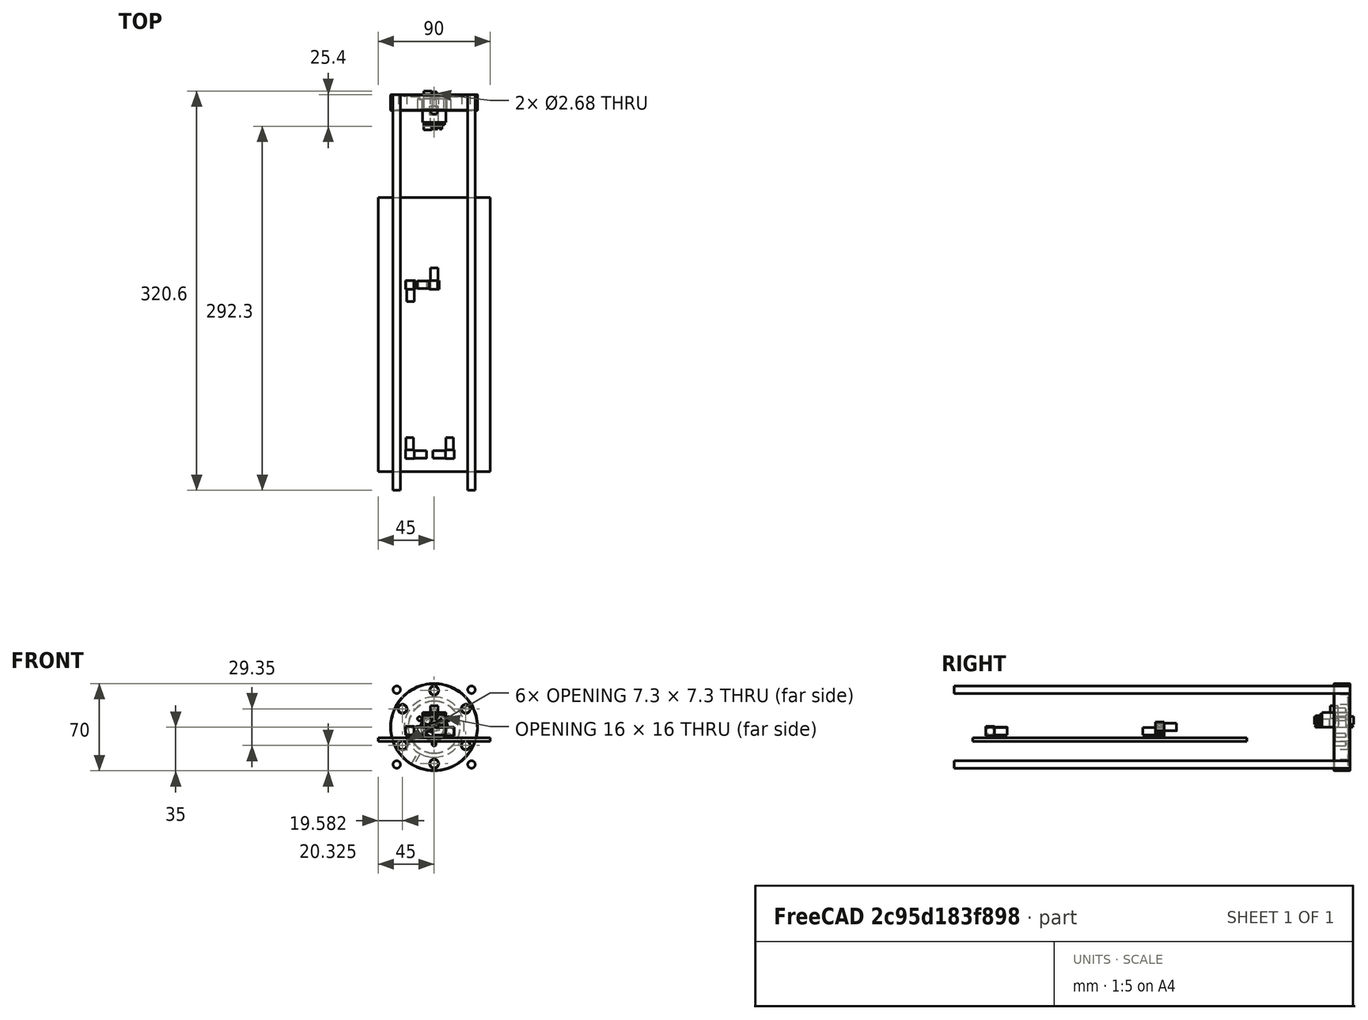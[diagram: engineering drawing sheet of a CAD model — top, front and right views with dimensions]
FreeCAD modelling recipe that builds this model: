
FCSTD DOCUMENT  (FreeCAD 0.20R29603 (Git))
Label: MechanicalCF35Mount_Assembly
License: All rights reserved
LicenseURL: http://en.wikipedia.org/wiki/All_rights_reserved
objects: Part::Feature×22, App::Link×16, Part::Compound×9, Part::Cylinder×4, Part::Box×1
note: 36 computed .brp shape members not serialized (recipe doc carries the construction recipe); baked Part::Feature solids carry a one-line shape summary decoded from their .brp
EXTERNAL_REF file=MechanicalCF35Mount001.FCStd obj=Fillet_solid
EXTERNAL_REF file=MechanicalCF35Mount002.FCStd obj=Cut001_solid
EXTERNAL_REF file=MechanicalCF35Mount003.FCStd obj=Cut001_solid
EXTERNAL_REF file=MechanicalCF35Mount004.FCStd obj=Cut_solid
EXTERNAL_REF file=../../MiniCircuits/GC957.FCStd obj=Fusion001_solid
EXTERNAL_REF file=../../MiniCircuits/FF99.FCStd obj=Fusion_solid
EXTERNAL_REF file=../../MiniCircuits/SMA-L.FCStd obj=Fusion_solid
EXTERNAL_REF file=MechanicalCF35Mount005.FCStd obj=Common_solid

FEATURE [App::Link] Link  label="Frontplane"
  LinkedObject = -> <external MechanicalCF35Mount001.FCStd>#Fillet_solid
FEATURE [Part::Cylinder] Cylinder  label="Zylinder"
  Angle = 360
  AttacherType = Attacher::AttachEngine3D
  FirstAngle = 0
  Height = 317.7
  Placement = pos=(-30,12.7,-30) rot=(1,0,0;1.5708rad)
  Radius = 3
  SecondAngle = 0
FEATURE [Part::Cylinder] Cylinder001  label="Zylinder001"
  Angle = 360
  AttacherType = Attacher::AttachEngine3D
  FirstAngle = 0
  Height = 317.7
  Placement = pos=(-30,12.7,-30) rot=(1,0,0;1.5708rad)
  Radius = 3
  SecondAngle = 0
FEATURE [Part::Compound] Compound
  Links = -> [Cylinder001]
  Placement = pos=(0,0,0) rot=(0,1,0;1.5708rad)
FEATURE [Part::Cylinder] Cylinder002  label="Zylinder002"
  Angle = 360
  AttacherType = Attacher::AttachEngine3D
  FirstAngle = 0
  Height = 317.7
  Placement = pos=(-30,12.7,-30) rot=(1,0,0;1.5708rad)
  Radius = 3
  SecondAngle = 0
FEATURE [Part::Compound] Compound001
  Links = -> [Cylinder002]
  Placement = pos=(0,0,0) rot=(0,1,0;3.14159rad)
FEATURE [Part::Cylinder] Cylinder003  label="Zylinder003"
  Angle = 360
  AttacherType = Attacher::AttachEngine3D
  FirstAngle = 0
  Height = 317.7
  Placement = pos=(-30,12.7,-30) rot=(1,0,0;1.5708rad)
  Radius = 3
  SecondAngle = 0
FEATURE [Part::Compound] Compound002
  Links = -> [Cylinder003]
  Placement = pos=(0,0,0) rot=(0,1,0;4.71239rad)
FEATURE [Part::Compound] Compound003  label="ThreadedRodsM6"
  Links = -> [Compound002,Compound,Compound001,Cylinder]
FEATURE [App::Link] Link005  label="Backplane"
  LinkPlacement = pos=(0,-302,0) rot=(0,0,1;0rad)
  LinkedObject = -> <external MechanicalCF35Mount002.FCStd>#Cut001_solid
  Placement = pos=(0,-302,0) rot=(0,0,1;0rad)
FEATURE [App::Link] Link006  label="Coversheet"
  LinkedObject = -> <external MechanicalCF35Mount003.FCStd>#Cut001_solid
FEATURE [App::Link] Link007  label="Bottomplane"
  LinkPlacement = pos=(0,0,-101.8) rot=(0,0,1;0rad)
  LinkedObject = -> <external MechanicalCF35Mount004.FCStd>#Cut_solid
  Placement = pos=(0,0,-101.8) rot=(0,0,1;0rad)
FEATURE [Part::Feature] Solid  label="Hositrad_CFA35-16D"
  shape: bbox 70 x 12.7 x 70 mm, 88 faces (baked)
FEATURE [Part::Feature] _7192_01_CF
  shape: bbox 33.78 x 40.23 x 14.22 mm, 39 faces, 0 solids (baked)
FEATURE [Part::Feature] _7192_01_CF001
  Placement = pos=(0,0,-39.0113) rot=(1,0,0;1.5708rad)
  shape: bbox 14 x 7.506 x 26.34 mm, 46 faces, 0 solids (baked)
FEATURE [Part::Feature] _7192_01_CF002
  Placement = pos=(0,0,-58.2625) rot=(-0.03621,0.706643,0.706643;3.21398rad)
  shape: bbox 18.12 x 10.39 x 7.838 mm, 29 faces, 0 solids (baked)
FEATURE [Part::Feature] _7192_01_CF003
  Placement = pos=(0,0,-42.2965) rot=(0.8891,-0.323652,-0.323652;1.68807rad)
  shape: bbox 16.99 x 16.03 x 5.603 mm, 25 faces, 0 solids (baked)
FEATURE [Part::Feature] _7192_01_CF004
  Placement = pos=(0,0,-35.56) rot=(0,0.707107,-0.707107;3.14159rad)
  shape: bbox 22.78 x 12.72 x 33.85 mm, 35 faces, 0 solids (baked)
FEATURE [Part::Feature] _7192_01_CF005
  Placement = pos=(0,0,-36.7339) rot=(0.997746,-0.047454,-0.047454;1.57305rad)
  shape: bbox 7.007 x 7.007 x 0.8128 mm, 6 faces, 0 solids (baked)
FEATURE [Part::Feature] _7192_01_CF006
  Placement = pos=(0,0,-66.0654) rot=(0.57735,0.57735,0.57735;2.0944rad)
  shape: bbox 2.416 x 2.416 x 39.37 mm, 29 faces, 0 solids (baked)
FEATURE [Part::Feature] _7192_01_CF007
  Placement = pos=(0,0,-32.2253) rot=(-0.196732,-0.693288,0.693288;2.75309rad)
  shape: bbox 26.96 x 26.96 x 13.28 mm, 55 faces, 0 solids (baked)
FEATURE [Part::Feature] _7192_01_CF008
  Placement = pos=(0,0,-46.1699) rot=(-0.196732,-0.693288,0.693288;2.75309rad)
  shape: bbox 34.28 x 29.27 x 4.775 mm, 16 faces, 0 solids (baked)
FEATURE [Part::Feature] _7192_01_CF009
  Placement = pos=(0,0,-22.86) rot=(-0.196732,-0.693288,0.693288;2.75309rad)
  shape: bbox 24.3 x 24.3 x 12.6 mm, 19 faces, 0 solids (baked)
FEATURE [Part::Feature] _7192_01_CF010
  Placement = pos=(0,0,-12.7) rot=(-0.196732,-0.693288,0.693288;2.75309rad)
  shape: bbox 26.42 x 26.42 x 12.7 mm, 14 faces, 0 solids (baked)
FEATURE [Part::Feature] _7192_01_CF011
  Placement = pos=(0,0,-42.1821) rot=(-0.196732,-0.693288,0.693288;2.75309rad)
  shape: bbox 43.95 x 37.52 x 5.044 mm, 27 faces, 0 solids (baked)
FEATURE [Part::Feature] _7192_01_CF012
  Placement = pos=(0,0,-35.56) rot=(0.079728,0.704856,0.704856;2.98247rad)
  shape: bbox 15.4 x 15.4 x 39.12 mm, 6 faces, 0 solids (baked)
FEATURE [Part::Feature] _7192_01_CF013
  Placement = pos=(0,0,-26.6954) rot=(0.165786,0.697322,0.697322;2.81301rad)
  shape: bbox 5.339 x 4.281 x 34.06 mm, 6 faces, 0 solids (baked)
FEATURE [Part::Feature] _7192_01_CF014
  Placement = pos=(0,0,6.7564) rot=(0.205998,0.691941,-0.691941;3.54791rad)
  shape: bbox 9.907 x 7.446 x 1.311 mm, 4 faces, 0 solids (baked)
FEATURE [Part::Feature] _7192_01_CF015
  Placement = pos=(0,0,-7.9756) rot=(1,0,0;1.5708rad)
  shape: bbox 22.78 x 12.72 x 22.32 mm, 35 faces, 0 solids (baked)
FEATURE [Part::Feature] _7192_01_CF016
  Placement = pos=(0,0,22.3805) rot=(0.205998,0.691941,-0.691941;3.54791rad)
  shape: bbox 3.344 x 3.344 x 15.27 mm, 29 faces, 0 solids (baked)
FEATURE [Part::Feature] _7192_01_CF017
  Placement = pos=(0,0,6.7564) rot=(1,0,0;1.5708rad)
  shape: bbox 10.8 x 10.8 x 1.524 mm, 10 faces, 0 solids (baked)
FEATURE [Part::Compound] Compound004  label="CF16BNCFeedthrough"
  Links = -> [_7192_01_CF,_7192_01_CF001,_7192_01_CF002,_7192_01_CF003,_7192_01_CF004,_7192_01_CF005,_7192_01_CF006,_7192_01_CF007,_7192_01_CF008,_7192_01_CF009,_7192_01_CF010,_7192_01_CF011,_7192_01_CF012,_7192_01_CF013,_7192_01_CF014,_7192_01_CF015,_7192_01_CF016,_7192_01_CF017]
  Placement = pos=(0,0,0) rot=(-1,0,0;1.5708rad)
FEATURE [App::Link] Link008  label="Preamp1"
  LinkPlacement = pos=(-14.5,-165,-8.45) rot=(0,0,1;0rad)
  LinkedObject = -> <external ../../MiniCircuits/GC957.FCStd>#Fusion001_solid
  Placement = pos=(-14.5,-165,-8.45) rot=(0,0,1;0rad)
FEATURE [App::Link] Link009  label="SHP-175"
  LinkPlacement = pos=(0,-86,0) rot=(1,0,0;1.5708rad)
  LinkedObject = -> <external ../../MiniCircuits/FF99.FCStd>#Fusion_solid
  Placement = pos=(0,-86,0) rot=(1,0,0;1.5708rad)
FEATURE [App::Link] Link010  label="Fusion (Solid)"
  LinkPlacement = pos=(0,-140,-3.5) rot=(0,0,1;3.14159rad)
  LinkedObject = -> <external ../../MiniCircuits/SMA-L.FCStd>#Fusion_solid
  Placement = pos=(0,-140,-3.5) rot=(0,0,1;3.14159rad)
FEATURE [Part::Compound] Compound005  label="SMAL001"
  Links = -> [Link010]
  Placement = pos=(0,0,0) rot=(0,-1,0;1.74533rad)
FEATURE [App::Link] Link011  label="Fusion (Solid)001"
  LinkPlacement = pos=(0,-140,-3.5) rot=(0,0,1;0rad)
  LinkedObject = -> Fusion_solid
  Placement = pos=(0,-140,-3.5) rot=(0,0,1;0rad)
FEATURE [Part::Compound] Compound006  label="SMAL002"
  Links = -> [Link011]
  Placement = pos=(-19,0,-3.45) rot=(0,1,0;1.39626rad)
FEATURE [Part::Feature] Fusion_solid  label="Fusion (Solid)002"
  shape: bbox 7 x 17 x 17 mm, 12 faces (baked)
FEATURE [App::Link] Link012  label="Preamp002"
  LinkPlacement = pos=(-14.5,-207,-8.45) rot=(0,0,1;0rad)
  LinkedObject = -> Fusion001_solid
  Placement = pos=(-14.5,-207,-8.45) rot=(0,0,1;0rad)
FEATURE [Part::Feature] Fusion001_solid  label="Fusion001 (Solid)"
  shape: bbox 18.8 x 31.2 x 11.61 mm, 42 faces (baked)
FEATURE [Part::Feature] Fusion001_solid001  label="Fusion001 (Solid)001"
  shape: bbox 18.8 x 31.2 x 11.61 mm, 42 faces (baked)
FEATURE [App::Link] Link013  label="Preamp003"
  LinkPlacement = pos=(-14.5,-248,-8.45) rot=(0,0,1;0rad)
  LinkedObject = -> Fusion001_solid001
  Placement = pos=(-14.5,-248,-8.45) rot=(0,0,1;0rad)
FEATURE [App::Link] Link014  label="Fusion (Solid)003"
  LinkPlacement = pos=(0,0,0) rot=(0,0,1;3.14159rad)
  LinkedObject = -> <external ../../MiniCircuits/SMA-L.FCStd>#Fusion_solid
  Placement = pos=(0,0,0) rot=(0,0,1;3.14159rad)
FEATURE [Part::Compound] Compound007  label="SMAL003"
  Links = -> [Link014]
  Placement = pos=(-23,-276,-3) rot=(0,1,0;1.5708rad)
FEATURE [App::Link] Link015  label="Fusion (Solid)004"
  LinkPlacement = pos=(0,0,0) rot=(0,1,0;1.5708rad)
  LinkedObject = -> <external ../../MiniCircuits/SMA-L.FCStd>#Fusion_solid
  Placement = pos=(0,0,0) rot=(0,1,0;1.5708rad)
FEATURE [Part::Compound] Compound008
  Links = -> [Link015]
  Placement = pos=(16,-276,-3.5) rot=(0,0,1;3.14159rad)
FEATURE [Part::Box] Box  label="MountBoard"
  AttacherType = Attacher::AttachEngine3D
  Height = 2.8
  Length = 90
  Placement = pos=(-45,-290,-11.5) rot=(0,0,1;0rad)
  Width = 220
FEATURE [App::Link] Link016  label="Common (Solid)"
  LinkPlacement = pos=(0,-76,0) rot=(0,0,1;0rad)
  LinkedObject = -> <external MechanicalCF35Mount005.FCStd>#Common_solid
  Placement = pos=(0,-76,0) rot=(0,0,1;0rad)
FEATURE [App::Link] Link017  label="Common (Solid)001"
  LinkPlacement = pos=(0,-283,0) rot=(0,0,1;0rad)
  LinkedObject = -> <external MechanicalCF35Mount005.FCStd>#Common_solid
  Placement = pos=(0,-283,0) rot=(0,0,1;0rad)
FEATURE [App::Link] Link018  label="Common (Solid)002"
  LinkPlacement = pos=(0,-144,0) rot=(0,0,1;0rad)
  LinkedObject = -> <external MechanicalCF35Mount005.FCStd>#Common_solid
  Placement = pos=(0,-144,0) rot=(0,0,1;0rad)
FEATURE [App::Link] Link019  label="Common (Solid)003"
  LinkPlacement = pos=(0,-215,0) rot=(0,0,1;0rad)
  LinkedObject = -> <external MechanicalCF35Mount005.FCStd>#Common_solid
  Placement = pos=(0,-215,0) rot=(0,0,1;0rad)

RESOLVED EXTERNAL PARTS (link-assembly join: the EXTERNAL_REF files above that resolve inside this repo's crawl, each included once):
---- part MechanicalCF35Mount001.FCStd = doc fcstd_43c363c283f8 ----
FCSTD DOCUMENT  (FreeCAD 0.20R29603 (Git))
Label: MechanicalCF35Mount001
License: All rights reserved
LicenseURL: http://en.wikipedia.org/wiki/All_rights_reserved
objects: Part::Feature×20, Part::Cylinder×15, TechDraw::DrawViewDimension×13, Part::Compound×12, TechDraw::DrawProjGroupItem×5, Part::Cut×4, Part::Box×1, Part::Fillet×1, TechDraw::DrawSVGTemplate×1, TechDraw::DrawProjGroup×1, TechDraw::DrawPage×1
note: 53 computed .brp shape members not serialized (recipe doc carries the construction recipe); baked Part::Feature solids carry a one-line shape summary decoded from their .brp

FEATURE [Part::Feature] Solid  label="Hositrad_CFA35-16D"
  shape: bbox 70 x 12.7 x 70 mm, 88 faces (baked)
FEATURE [Part::Feature] _7192_01_CF
  shape: bbox 33.78 x 40.23 x 14.22 mm, 39 faces, 0 solids (baked)
FEATURE [Part::Feature] _7192_01_CF001
  Placement = pos=(0,0,-39.0113) rot=(1,0,0;1.5708rad)
  shape: bbox 14 x 7.506 x 26.34 mm, 46 faces, 0 solids (baked)
FEATURE [Part::Feature] _7192_01_CF002
  Placement = pos=(0,0,-58.2625) rot=(-0.03621,0.706643,0.706643;3.21398rad)
  shape: bbox 18.12 x 10.39 x 7.838 mm, 29 faces, 0 solids (baked)
FEATURE [Part::Feature] _7192_01_CF003
  Placement = pos=(0,0,-42.2965) rot=(0.8891,-0.323652,-0.323652;1.68807rad)
  shape: bbox 16.99 x 16.03 x 5.603 mm, 25 faces, 0 solids (baked)
FEATURE [Part::Feature] _7192_01_CF004
  Placement = pos=(0,0,-35.56) rot=(0,0.707107,-0.707107;3.14159rad)
  shape: bbox 22.78 x 12.72 x 33.85 mm, 35 faces, 0 solids (baked)
FEATURE [Part::Feature] _7192_01_CF005
  Placement = pos=(0,0,-36.7339) rot=(0.997746,-0.047454,-0.047454;1.57305rad)
  shape: bbox 7.007 x 7.007 x 0.8128 mm, 6 faces, 0 solids (baked)
FEATURE [Part::Feature] _7192_01_CF006
  Placement = pos=(0,0,-66.0654) rot=(0.57735,0.57735,0.57735;2.0944rad)
  shape: bbox 2.416 x 2.416 x 39.37 mm, 29 faces, 0 solids (baked)
FEATURE [Part::Feature] _7192_01_CF007
  Placement = pos=(0,0,-32.2253) rot=(0.196732,0.693288,-0.693288;3.5301rad)
  shape: bbox 26.96 x 26.96 x 13.28 mm, 55 faces, 0 solids (baked)
FEATURE [Part::Feature] _7192_01_CF008
  Placement = pos=(0,0,-46.1699) rot=(0.196732,0.693288,-0.693288;3.5301rad)
  shape: bbox 34.28 x 29.27 x 4.775 mm, 16 faces, 0 solids (baked)
FEATURE [Part::Feature] _7192_01_CF009
  Placement = pos=(0,0,-22.86) rot=(0.196732,0.693288,-0.693288;3.5301rad)
  shape: bbox 24.3 x 24.3 x 12.6 mm, 19 faces, 0 solids (baked)
FEATURE [Part::Feature] _7192_01_CF010
  Placement = pos=(0,0,-12.7) rot=(0.196732,0.693288,-0.693288;3.5301rad)
  shape: bbox 26.42 x 26.42 x 12.7 mm, 14 faces, 0 solids (baked)
FEATURE [Part::Feature] _7192_01_CF011
  Placement = pos=(0,0,-42.1821) rot=(0.196732,0.693288,-0.693288;3.5301rad)
  shape: bbox 43.95 x 37.52 x 5.044 mm, 27 faces, 0 solids (baked)
FEATURE [Part::Feature] _7192_01_CF012
  Placement = pos=(0,0,-35.56) rot=(0.079728,0.704856,0.704856;2.98247rad)
  shape: bbox 15.4 x 15.4 x 39.12 mm, 6 faces, 0 solids (baked)
FEATURE [Part::Feature] _7192_01_CF013
  Placement = pos=(0,0,-26.6954) rot=(0.165786,0.697322,0.697322;2.81301rad)
  shape: bbox 5.339 x 4.281 x 34.06 mm, 6 faces, 0 solids (baked)
FEATURE [Part::Feature] _7192_01_CF014
  Placement = pos=(0,0,6.7564) rot=(0.205998,0.691941,-0.691941;3.54791rad)
  shape: bbox 9.907 x 7.446 x 1.311 mm, 4 faces, 0 solids (baked)
FEATURE [Part::Feature] _7192_01_CF015
  Placement = pos=(0,0,-7.9756) rot=(1,0,0;1.5708rad)
  shape: bbox 22.78 x 12.72 x 22.32 mm, 35 faces, 0 solids (baked)
FEATURE [Part::Feature] _7192_01_CF016
  Placement = pos=(0,0,22.3805) rot=(0.205998,0.691941,-0.691941;3.54791rad)
  shape: bbox 3.344 x 3.344 x 15.27 mm, 29 faces, 0 solids (baked)
FEATURE [Part::Feature] _7192_01_CF017
  Placement = pos=(0,0,6.7564) rot=(1,0,0;1.5708rad)
  shape: bbox 10.8 x 10.8 x 1.524 mm, 10 faces, 0 solids (baked)
FEATURE [Part::Compound] Compound  label="CF16BNCFeedthrough"
  Links = -> [_7192_01_CF,_7192_01_CF001,_7192_01_CF002,_7192_01_CF003,_7192_01_CF004,_7192_01_CF005,_7192_01_CF006,_7192_01_CF007,_7192_01_CF008,_7192_01_CF009,_7192_01_CF010,_7192_01_CF011,_7192_01_CF012,_7192_01_CF013,_7192_01_CF014,_7192_01_CF015,_7192_01_CF016,_7192_01_CF017]
  Placement = pos=(0,0,0) rot=(-1,0,0;1.5708rad)
FEATURE [Part::Box] Box  label="Würfel"
  AttacherType = Attacher::AttachEngine3D
  Height = 100
  Length = 100
  Placement = pos=(-50,0,-50) rot=(0,0,1;0rad)
  Width = 12.7
FEATURE [Part::Cylinder] Cylinder  label="Zylinder"
  Angle = 360
  AttacherType = Attacher::AttachEngine3D
  FirstAngle = 0
  Height = 12.7
  Placement = pos=(0,12.7,0) rot=(1,0,0;1.5708rad)
  Radius = 35.5
  SecondAngle = 0
FEATURE [Part::Cut] Cut
  Base = -> Box
  Tool = -> Cylinder
FEATURE [Part::Cylinder] Cylinder001  label="Zylinder001"
  Angle = 360
  AttacherType = Attacher::AttachEngine3D
  FirstAngle = 0
  Height = 100
  Placement = pos=(0,6.35,-50) rot=(0,0,1;0rad)
  Radius = 2.46
  SecondAngle = 0
FEATURE [Part::Cylinder] Cylinder002  label="Zylinder002"
  Angle = 360
  AttacherType = Attacher::AttachEngine3D
  FirstAngle = 0
  Height = 100
  Placement = pos=(0,6.35,-50) rot=(0,0,1;0rad)
  Radius = 2.46
  SecondAngle = 0
FEATURE [Part::Compound] Compound001
  Links = -> [Cylinder002]
  Placement = pos=(0,0,0) rot=(0,1,0;1.5708rad)
FEATURE [Part::Compound] Compound002  label="SetscrewCoreholes"
  Links = -> [Compound001,Cylinder001]
FEATURE [Part::Cut] Cut001
  Base = -> Cut
  Tool = -> Compound002
FEATURE [Part::Cylinder] Cylinder003  label="Zylinder003"
  Angle = 360
  AttacherType = Attacher::AttachEngine3D
  FirstAngle = 0
  Height = 12
  Placement = pos=(-30,6.3,-50) rot=(0,0,1;0rad)
  Radius = 2.46
  SecondAngle = 0
FEATURE [Part::Cylinder] Cylinder004  label="Zylinder004"
  Angle = 360
  AttacherType = Attacher::AttachEngine3D
  FirstAngle = 0
  Height = 12
  Placement = pos=(30,6.3,-50) rot=(0,0,1;0rad)
  Radius = 2.46
  SecondAngle = 0
FEATURE [Part::Compound] Compound003
  Links = -> [Cylinder003,Cylinder004]
FEATURE [Part::Cylinder] Cylinder005  label="Zylinder005"
  Angle = 360
  AttacherType = Attacher::AttachEngine3D
  FirstAngle = 0
  Height = 12
  Placement = pos=(-30,6.3,-50) rot=(0,0,1;0rad)
  Radius = 2.46
  SecondAngle = 0
FEATURE [Part::Cylinder] Cylinder006  label="Zylinder006"
  Angle = 360
  AttacherType = Attacher::AttachEngine3D
  FirstAngle = 0
  Height = 12
  Placement = pos=(30,6.3,-50) rot=(0,0,1;0rad)
  Radius = 2.46
  SecondAngle = 0
FEATURE [Part::Compound] Compound004
  Links = -> [Cylinder005,Cylinder006]
  Placement = pos=(0,0,0) rot=(0,-1,0;1.5708rad)
FEATURE [Part::Cylinder] Cylinder007  label="Zylinder007"
  Angle = 360
  AttacherType = Attacher::AttachEngine3D
  FirstAngle = 0
  Height = 12
  Placement = pos=(-30,6.3,-50) rot=(0,0,1;0rad)
  Radius = 2.46
  SecondAngle = 0
FEATURE [Part::Cylinder] Cylinder008  label="Zylinder008"
  Angle = 360
  AttacherType = Attacher::AttachEngine3D
  FirstAngle = 0
  Height = 12
  Placement = pos=(30,6.3,-50) rot=(0,0,1;0rad)
  Radius = 2.46
  SecondAngle = 0
FEATURE [Part::Compound] Compound005
  Links = -> [Cylinder007,Cylinder008]
  Placement = pos=(0,0,0) rot=(0,1,0;3.14159rad)
FEATURE [Part::Cylinder] Cylinder009  label="Zylinder009"
  Angle = 360
  AttacherType = Attacher::AttachEngine3D
  FirstAngle = 0
  Height = 12
  Placement = pos=(-30,6.3,-50) rot=(0,0,1;0rad)
  Radius = 2.46
  SecondAngle = 0
FEATURE [Part::Cylinder] Cylinder010  label="Zylinder010"
  Angle = 360
  AttacherType = Attacher::AttachEngine3D
  FirstAngle = 0
  Height = 12
  Placement = pos=(30,6.3,-50) rot=(0,0,1;0rad)
  Radius = 2.46
  SecondAngle = 0
FEATURE [Part::Compound] Compound006
  Links = -> [Cylinder009,Cylinder010]
  Placement = pos=(0,0,0) rot=(0,1,0;-4.71239rad)
FEATURE [Part::Compound] Compound007  label="M6Mountscrews"
  Links = -> [Compound003,Compound004,Compound005,Compound006]
FEATURE [Part::Cut] Cut002
  Base = -> Cut001
  Tool = -> Compound007
FEATURE [Part::Cylinder] Cylinder011  label="Zylinder011"
  Angle = 360
  AttacherType = Attacher::AttachEngine3D
  FirstAngle = 0
  Height = 300
  Placement = pos=(30,12.7,30) rot=(1,0,0;1.5708rad)
  Radius = 2.38
  SecondAngle = 0
FEATURE [Part::Cylinder] Cylinder012  label="Zylinder012"
  Angle = 360
  AttacherType = Attacher::AttachEngine3D
  FirstAngle = 0
  Height = 300
  Placement = pos=(30,12.7,30) rot=(1,0,0;1.5708rad)
  Radius = 2.38
  SecondAngle = 0
FEATURE [Part::Compound] Compound008
  Links = -> [Cylinder012]
  Placement = pos=(0,0,0) rot=(0,1,0;1.5708rad)
FEATURE [Part::Cylinder] Cylinder013  label="Zylinder013"
  Angle = 360
  AttacherType = Attacher::AttachEngine3D
  FirstAngle = 0
  Height = 300
  Placement = pos=(30,12.7,30) rot=(1,0,0;1.5708rad)
  Radius = 2.38
  SecondAngle = 0
FEATURE [Part::Compound] Compound009
  Links = -> [Cylinder013]
  Placement = pos=(0,0,0) rot=(0,1,0;3.14159rad)
FEATURE [Part::Cylinder] Cylinder014  label="Zylinder014"
  Angle = 360
  AttacherType = Attacher::AttachEngine3D
  FirstAngle = 0
  Height = 300
  Placement = pos=(30,12.7,30) rot=(1,0,0;1.5708rad)
  Radius = 2.38
  SecondAngle = 0
FEATURE [Part::Compound] Compound010
  Links = -> [Cylinder014]
  Placement = pos=(0,0,0) rot=(0,-1,0;1.5708rad)
FEATURE [Part::Compound] Compound014  label="M6ThreadRods"
  Links = -> [Cylinder011,Compound008,Compound009,Compound010]
FEATURE [Part::Cut] Cut003
  Base = -> Cut002
  Tool = -> Compound014
FEATURE [Part::Fillet] Fillet
  Base = -> Cut003
  Edges = 2 edges r=2: [Edge2,Edge3]
FEATURE [Part::Feature] Fillet_solid  label="Fillet (Solid)"
  shape: bbox 100 x 12.7 x 100 mm, 33 faces (baked)
FEATURE [TechDraw::DrawSVGTemplate] Template
  EditableTexts = Designed_by_Name=Thomas Spielauer; FC-Date=2023-07-05; FC-SC=mm; FC-SH=01; FC-Title=CF40 electronics housing; Subtitle=Front plate
  Height = 210
  Orientation = 1
  Width = 297
FEATURE [TechDraw::DrawProjGroupItem] ProjItem  label="Front"
  CoarseView = false
  Direction = (0,-1,0)
  Focus = 100
  HardHidden = false
  IsoCount = 0
  IsoHidden = false
  IsoVisible = false
  LockPosition = true
  Perspective = false
  Rotation = 0
  RotationVector = (0,0,1)
  ScaleType = 2
  SeamHidden = false
  SeamVisible = true
  SmoothHidden = false
  SmoothVisible = true
  Source = -> [Fillet]
  Type = 0
  X = 0
  XDirection = (0,0,1)
  Y = 0
FEATURE [TechDraw::DrawProjGroupItem] ProjItem001  label="Right"
  CoarseView = false
  Direction = (0,-1e-16,1)
  Focus = 100
  HardHidden = false
  IsoCount = 0
  IsoHidden = false
  IsoVisible = false
  LockPosition = false
  Perspective = false
  Rotation = 0
  RotationVector = (1,0,0)
  ScaleType = 2
  SeamHidden = false
  SeamVisible = true
  SmoothHidden = false
  SmoothVisible = true
  Source = -> [Fillet]
  Type = 2
  X = -67.6611
  XDirection = (0,1,1e-16)
  Y = 0
FEATURE [TechDraw::DrawProjGroupItem] ProjItem002  label="Bottom"
  CoarseView = false
  Direction = (1,0,0)
  Focus = 100
  HardHidden = false
  IsoCount = 0
  IsoHidden = false
  IsoVisible = false
  LockPosition = false
  Perspective = false
  Rotation = 0
  RotationVector = (1,0,0)
  ScaleType = 2
  SeamHidden = false
  SeamVisible = true
  SmoothHidden = false
  SmoothVisible = true
  Source = -> [Fillet]
  Type = 5
  X = 0
  XDirection = (0,0,1)
  Y = 73.816
FEATURE [TechDraw::DrawProjGroupItem] ProjItem003  label="Left"
  CoarseView = false
  Direction = (0,-1e-16,-1)
  Focus = 100
  HardHidden = false
  IsoCount = 0
  IsoHidden = false
  IsoVisible = false
  LockPosition = false
  Perspective = false
  Rotation = 0
  RotationVector = (1,0,0)
  ScaleType = 2
  SeamHidden = false
  SeamVisible = true
  SmoothHidden = false
  SmoothVisible = true
  Source = -> [Fillet]
  Type = 1
  X = 105.155
  XDirection = (0,-1,1e-16)
  Y = 0
FEATURE [TechDraw::DrawProjGroupItem] ProjItem004  label="Top"
  CoarseView = false
  Direction = (-1,0,0)
  Focus = 100
  HardHidden = false
  IsoCount = 0
  IsoHidden = false
  IsoVisible = false
  LockPosition = false
  Perspective = false
  Rotation = 0
  RotationVector = (1,0,0)
  ScaleType = 2
  SeamHidden = false
  SeamVisible = true
  SmoothHidden = false
  SmoothVisible = true
  Source = -> [Fillet]
  Type = 4
  X = 0
  XDirection = (0,0,1)
  Y = -75.3562
FEATURE [TechDraw::DrawProjGroup] ProjGroup
  Anchor = -> ProjItem
  AutoDistribute = true
  LockPosition = false
  ProjectionType = 0
  Rotation = 0
  ScaleType = 0
  Source = -> [Fillet]
  Views = -> [ProjItem,ProjItem001,ProjItem002,ProjItem003,ProjItem004]
  X = 91.0868
  Y = 118.279
  spacingX = 0
  spacingY = 0
FEATURE [TechDraw::DrawViewDimension] Dimension
  AngleOverride = false
  Arbitrary = false
  ArbitraryTolerances = false
  EqualTolerance = true
  ExtensionAngle = 0
  FormatSpec = %.2w
  FormatSpecOverTolerance = %+.2w
  FormatSpecUnderTolerance = %+.2w
  Inverted = false
  LineAngle = 0
  LockPosition = false
  MeasureType = 1
  OverTolerance = 0
  References2D = -> [ProjItem003]
  Rotation = 0
  ScaleType = 0
  TheoreticalExact = false
  Type = 0
  UnderTolerance = 0
  X = 27.7422
  Y = 2.49993
FEATURE [TechDraw::DrawViewDimension] Dimension001
  AngleOverride = false
  Arbitrary = false
  ArbitraryTolerances = false
  EqualTolerance = true
  ExtensionAngle = 0
  FormatSpec = %.2w
  FormatSpecOverTolerance = %+.2w
  FormatSpecUnderTolerance = %+.2w
  Inverted = false
  LineAngle = 0
  LockPosition = false
  MeasureType = 1
  OverTolerance = 0
  References2D = -> [ProjItem004]
  Rotation = 0
  ScaleType = 0
  TheoreticalExact = false
  Type = 0
  UnderTolerance = 0
  X = -0.515822
  Y = -20.0124
FEATURE [TechDraw::DrawViewDimension] Dimension002
  AngleOverride = false
  Arbitrary = false
  ArbitraryTolerances = false
  EqualTolerance = true
  ExtensionAngle = 0
  FormatSpec = ⌀%.2w
  FormatSpecOverTolerance = %+.2w
  FormatSpecUnderTolerance = %+.2w
  Inverted = false
  LineAngle = 0
  LockPosition = false
  MeasureType = 1
  OverTolerance = 0
  References2D = -> [ProjItem]
  Rotation = 0
  ScaleType = 0
  TheoreticalExact = false
  Type = 5
  UnderTolerance = 0
  X = 0.325472
  Y = 8.03302
FEATURE [TechDraw::DrawViewDimension] Dimension003
  AngleOverride = false
  Arbitrary = false
  ArbitraryTolerances = false
  EqualTolerance = true
  ExtensionAngle = 0
  FormatSpec = ⌀%.2w (M6 4x)
  FormatSpecOverTolerance = %+.2w
  FormatSpecUnderTolerance = %+.2w
  Inverted = false
  LineAngle = 0
  LockPosition = false
  MeasureType = 1
  OverTolerance = 0
  References2D = -> [ProjItem]
  Rotation = 0
  ScaleType = 0
  TheoreticalExact = false
  Type = 5
  UnderTolerance = 0
  X = -23.9583
  Y = 40.0197
FEATURE [TechDraw::DrawViewDimension] Dimension004
  AngleOverride = false
  Arbitrary = false
  ArbitraryTolerances = false
  EqualTolerance = true
  ExtensionAngle = 0
  FormatSpec = %.2w
  FormatSpecOverTolerance = %+.2w
  FormatSpecUnderTolerance = %+.2w
  Inverted = false
  LineAngle = 0
  LockPosition = false
  MeasureType = 1
  OverTolerance = 0
  References2D = -> [ProjItem]
  Rotation = 0
  ScaleType = 0
  TheoreticalExact = false
  Type = 0
  UnderTolerance = 0
  X = 39.4213
  Y = 67.0173
FEATURE [TechDraw::DrawViewDimension] Dimension005
  AngleOverride = false
  Arbitrary = false
  ArbitraryTolerances = false
  EqualTolerance = true
  ExtensionAngle = 0
  FormatSpec = %.2w
  FormatSpecOverTolerance = %+.2w
  FormatSpecUnderTolerance = %+.2w
  Inverted = false
  LineAngle = 0
  LockPosition = false
  MeasureType = 1
  OverTolerance = 0
  References2D = -> [ProjItem]
  Rotation = 0
  ScaleType = 0
  TheoreticalExact = false
  Type = 0
  UnderTolerance = 0
  X = 34.38
  Y = 42.4999
FEATURE [TechDraw::DrawViewDimension] Dimension006
  AngleOverride = false
  Arbitrary = false
  ArbitraryTolerances = false
  EqualTolerance = true
  ExtensionAngle = 0
  FormatSpec = %.2w
  FormatSpecOverTolerance = %+.2w
  FormatSpecUnderTolerance = %+.2w
  Inverted = false
  LineAngle = 0
  LockPosition = false
  MeasureType = 1
  OverTolerance = 0
  References2D = -> [ProjItem]
  Rotation = 0
  ScaleType = 0
  TheoreticalExact = false
  Type = 0
  UnderTolerance = 0
  X = 71.4033
  Y = -19.5166
FEATURE [TechDraw::DrawViewDimension] Dimension007
  AngleOverride = false
  Arbitrary = false
  ArbitraryTolerances = false
  EqualTolerance = true
  ExtensionAngle = 0
  FormatSpec = %.2w
  FormatSpecOverTolerance = %+.2w
  FormatSpecUnderTolerance = %+.2w
  Inverted = false
  LineAngle = 0
  LockPosition = false
  MeasureType = 1
  OverTolerance = 0
  References2D = -> [ProjItem]
  Rotation = 0
  ScaleType = 0
  TheoreticalExact = false
  Type = 0
  UnderTolerance = 0
  X = -1.26969
  Y = 60.8859
FEATURE [TechDraw::DrawViewDimension] Dimension008
  AngleOverride = false
  Arbitrary = false
  ArbitraryTolerances = false
  EqualTolerance = true
  ExtensionAngle = 0
  FormatSpec = ⌀%.2w (M6 3x pro Seite)
  FormatSpecOverTolerance = %+.2w
  FormatSpecUnderTolerance = %+.2w
  Inverted = false
  LineAngle = 0
  LockPosition = false
  MeasureType = 1
  OverTolerance = 0
  References2D = -> [ProjItem003]
  Rotation = 0
  ScaleType = 0
  TheoreticalExact = false
  Type = 5
  UnderTolerance = 0
  X = 55.193
  Y = 36.5443
FEATURE [TechDraw::DrawViewDimension] Dimension009
  AngleOverride = false
  Arbitrary = false
  ArbitraryTolerances = false
  EqualTolerance = true
  ExtensionAngle = 0
  FormatSpec = %.2w
  FormatSpecOverTolerance = %+.2w
  FormatSpecUnderTolerance = %+.2w
  Inverted = false
  LineAngle = 0
  LockPosition = false
  MeasureType = 1
  OverTolerance = 0
  References2D = -> [ProjItem003]
  Rotation = 0
  ScaleType = 0
  TheoreticalExact = false
  Type = 0
  UnderTolerance = 0
  X = -14.0854
  Y = 64.8143
FEATURE [TechDraw::DrawViewDimension] Dimension010
  AngleOverride = false
  Arbitrary = false
  ArbitraryTolerances = false
  EqualTolerance = true
  ExtensionAngle = 0
  FormatSpec = %.2w
  FormatSpecOverTolerance = %+.2w
  FormatSpecUnderTolerance = %+.2w
  Inverted = false
  LineAngle = 0
  LockPosition = false
  MeasureType = 1
  OverTolerance = 0
  References2D = -> [ProjItem003]
  Rotation = 0
  ScaleType = 0
  TheoreticalExact = false
  Type = 0
  UnderTolerance = 0
  X = -20.8153
  Y = 17.1561
FEATURE [TechDraw::DrawViewDimension] Dimension011
  AngleOverride = false
  Arbitrary = false
  ArbitraryTolerances = false
  EqualTolerance = true
  ExtensionAngle = 0
  FormatSpec = %.2w
  FormatSpecOverTolerance = %+.2w
  FormatSpecUnderTolerance = %+.2w
  Inverted = false
  LineAngle = 0
  LockPosition = false
  MeasureType = 1
  OverTolerance = 0
  References2D = -> [ProjItem003]
  Rotation = 0
  ScaleType = 0
  TheoreticalExact = false
  Type = 0
  UnderTolerance = 0
  X = -20.7966
  Y = -12.5001
FEATURE [TechDraw::DrawViewDimension] Dimension012
  AngleOverride = false
  Arbitrary = false
  ArbitraryTolerances = false
  EqualTolerance = true
  ExtensionAngle = 0
  FormatSpec = %.2w
  FormatSpecOverTolerance = %+.2w
  FormatSpecUnderTolerance = %+.2w
  Inverted = false
  LineAngle = 0
  LockPosition = false
  MeasureType = 1
  OverTolerance = 0
  References2D = -> [ProjItem003]
  Rotation = 0
  ScaleType = 0
  TheoreticalExact = false
  Type = 0
  UnderTolerance = 0
  X = 15.28
  Y = -53.2031
FEATURE [TechDraw::DrawPage] Page
  KeepUpdated = true
  NextBalloonIndex = 1
  ProjectionType = 0
  Template = -> Template
  Views = -> [ProjGroup,Dimension,Dimension001,Dimension002,Dimension003,Dimension004,Dimension005,Dimension006,Dimension007,Dimension008,Dimension009,Dimension010,Dimension011,Dimension012]
---- part MechanicalCF35Mount002.FCStd = doc fcstd_76ff9047753c ----
FCSTD DOCUMENT  (FreeCAD 0.20R29603 (Git))
Label: MechanicalCF35Mount002
License: All rights reserved
LicenseURL: http://en.wikipedia.org/wiki/All_rights_reserved
objects: Part::Cylinder×12, Part::Compound×9, TechDraw::DrawViewDimension×9, TechDraw::DrawProjGroupItem×5, Part::Cut×2, Part::Box×1, Part::Feature×1, TechDraw::DrawSVGTemplate×1, TechDraw::DrawProjGroup×1, TechDraw::DrawPage×1
note: 25 computed .brp shape members not serialized (recipe doc carries the construction recipe); baked Part::Feature solids carry a one-line shape summary decoded from their .brp

FEATURE [Part::Box] Box  label="Würfel"
  AttacherType = Attacher::AttachEngine3D
  Height = 100
  Length = 100
  Placement = pos=(-50,0,-50) rot=(0,0,1;0rad)
  Width = 4
FEATURE [Part::Cylinder] Cylinder011  label="Zylinder011"
  Angle = 360
  AttacherType = Attacher::AttachEngine3D
  FirstAngle = 0
  Height = 300
  Placement = pos=(30,12.7,30) rot=(1,0,0;1.5708rad)
  Radius = 2.38
  SecondAngle = 0
FEATURE [Part::Cylinder] Cylinder012  label="Zylinder012"
  Angle = 360
  AttacherType = Attacher::AttachEngine3D
  FirstAngle = 0
  Height = 300
  Placement = pos=(30,12.7,30) rot=(1,0,0;1.5708rad)
  Radius = 2.38
  SecondAngle = 0
FEATURE [Part::Compound] Compound008
  Links = -> [Cylinder012]
  Placement = pos=(0,0,0) rot=(0,1,0;1.5708rad)
FEATURE [Part::Cylinder] Cylinder013  label="Zylinder013"
  Angle = 360
  AttacherType = Attacher::AttachEngine3D
  FirstAngle = 0
  Height = 300
  Placement = pos=(30,12.7,30) rot=(1,0,0;1.5708rad)
  Radius = 2.38
  SecondAngle = 0
FEATURE [Part::Compound] Compound009
  Links = -> [Cylinder013]
  Placement = pos=(0,0,0) rot=(0,1,0;3.14159rad)
FEATURE [Part::Cylinder] Cylinder014  label="Zylinder014"
  Angle = 360
  AttacherType = Attacher::AttachEngine3D
  FirstAngle = 0
  Height = 300
  Placement = pos=(30,12.7,30) rot=(1,0,0;1.5708rad)
  Radius = 2.38
  SecondAngle = 0
FEATURE [Part::Compound] Compound010
  Links = -> [Cylinder014]
  Placement = pos=(0,0,0) rot=(0,-1,0;1.5708rad)
FEATURE [Part::Compound] Compound014  label="M6ThreadRods"
  Links = -> [Cylinder011,Compound008,Compound009,Compound010]
FEATURE [Part::Cut] Cut
  Base = -> Box
  Tool = -> Compound014
FEATURE [Part::Cylinder] Cylinder  label="Zylinder"
  Angle = 360
  AttacherType = Attacher::AttachEngine3D
  FirstAngle = 0
  Height = 10
  Placement = pos=(30,2,40) rot=(0,0,1;0rad)
  Radius = 0.76
  SecondAngle = 0
FEATURE [Part::Cylinder] Cylinder015  label="Zylinder015"
  Angle = 360
  AttacherType = Attacher::AttachEngine3D
  FirstAngle = 0
  Height = 10
  Placement = pos=(-30,2,40) rot=(0,0,1;0rad)
  Radius = 0.76
  SecondAngle = 0
FEATURE [Part::Compound] Compound
  Links = -> [Cylinder,Cylinder015]
FEATURE [Part::Cylinder] Cylinder016  label="Zylinder016"
  Angle = 360
  AttacherType = Attacher::AttachEngine3D
  FirstAngle = 0
  Height = 10
  Placement = pos=(30,2,40) rot=(0,0,1;0rad)
  Radius = 0.76
  SecondAngle = 0
FEATURE [Part::Cylinder] Cylinder017  label="Zylinder017"
  Angle = 360
  AttacherType = Attacher::AttachEngine3D
  FirstAngle = 0
  Height = 10
  Placement = pos=(-30,2,40) rot=(0,0,1;0rad)
  Radius = 0.76
  SecondAngle = 0
FEATURE [Part::Compound] Compound015
  Links = -> [Cylinder016,Cylinder017]
  Placement = pos=(0,0,0) rot=(0,1,0;1.5708rad)
FEATURE [Part::Cylinder] Cylinder018  label="Zylinder018"
  Angle = 360
  AttacherType = Attacher::AttachEngine3D
  FirstAngle = 0
  Height = 10
  Placement = pos=(30,2,40) rot=(0,0,1;0rad)
  Radius = 0.76
  SecondAngle = 0
FEATURE [Part::Cylinder] Cylinder019  label="Zylinder019"
  Angle = 360
  AttacherType = Attacher::AttachEngine3D
  FirstAngle = 0
  Height = 10
  Placement = pos=(-30,2,40) rot=(0,0,1;0rad)
  Radius = 0.76
  SecondAngle = 0
FEATURE [Part::Compound] Compound016
  Links = -> [Cylinder018,Cylinder019]
  Placement = pos=(0,0,0) rot=(0,1,0;3.14159rad)
FEATURE [Part::Cylinder] Cylinder020  label="Zylinder020"
  Angle = 360
  AttacherType = Attacher::AttachEngine3D
  FirstAngle = 0
  Height = 10
  Placement = pos=(30,2,40) rot=(0,0,1;0rad)
  Radius = 0.76
  SecondAngle = 0
FEATURE [Part::Cylinder] Cylinder021  label="Zylinder021"
  Angle = 360
  AttacherType = Attacher::AttachEngine3D
  FirstAngle = 0
  Height = 10
  Placement = pos=(-30,2,40) rot=(0,0,1;0rad)
  Radius = 0.76
  SecondAngle = 0
FEATURE [Part::Compound] Compound017
  Links = -> [Cylinder020,Cylinder021]
  Placement = pos=(0,0,0) rot=(0,-1,0;1.5708rad)
FEATURE [Part::Compound] Compound018  label="M2Corehole"
  Links = -> [Compound017,Compound,Compound015,Compound016]
FEATURE [Part::Cut] Cut001
  Base = -> Cut
  Tool = -> Compound018
FEATURE [Part::Feature] Cut001_solid  label="Cut001 (Solid)"
  shape: bbox 100 x 4 x 100 mm, 26 faces (baked)
FEATURE [TechDraw::DrawSVGTemplate] Template
  EditableTexts = Designed_by_Name=Thomas Spielauer; FC-Date=2023-07-05; FC-SC=mm; FC-SH=01; FC-Title=CF40 electronics housing; Subtitle=Backplate
  Height = 210
  Orientation = 1
  Width = 297
FEATURE [TechDraw::DrawProjGroupItem] ProjItem  label="Front"
  CoarseView = false
  Direction = (0,1,0)
  Focus = 100
  HardHidden = false
  IsoCount = 0
  IsoHidden = false
  IsoVisible = false
  LockPosition = true
  Perspective = false
  Rotation = 0
  RotationVector = (0,0,-1)
  ScaleType = 2
  SeamHidden = false
  SeamVisible = true
  SmoothHidden = false
  SmoothVisible = true
  Source = -> [Cut001]
  Type = 0
  X = 0
  XDirection = (0,0,-1)
  Y = 0
FEATURE [TechDraw::DrawProjGroupItem] ProjItem001  label="Right"
  CoarseView = false
  Direction = (0,1e-16,-1)
  Focus = 100
  HardHidden = false
  IsoCount = 0
  IsoHidden = false
  IsoVisible = false
  LockPosition = false
  Perspective = false
  Rotation = 0
  RotationVector = (1,0,0)
  ScaleType = 2
  SeamHidden = false
  SeamVisible = true
  SmoothHidden = false
  SmoothVisible = true
  Source = -> [Cut001]
  Type = 2
  X = -67.1947
  XDirection = (0,-1,-1e-16)
  Y = 0
FEATURE [TechDraw::DrawProjGroupItem] ProjItem002  label="Left"
  CoarseView = false
  Direction = (0,1e-16,1)
  Focus = 100
  HardHidden = false
  IsoCount = 0
  IsoHidden = false
  IsoVisible = false
  LockPosition = false
  Perspective = false
  Rotation = 0
  RotationVector = (1,0,0)
  ScaleType = 2
  SeamHidden = false
  SeamVisible = true
  SmoothHidden = false
  SmoothVisible = true
  Source = -> [Cut001]
  Type = 1
  X = 75.0685
  XDirection = (0,1,-1e-16)
  Y = 0
FEATURE [TechDraw::DrawProjGroupItem] ProjItem003  label="Bottom"
  CoarseView = false
  Direction = (1,0,0)
  Focus = 100
  HardHidden = false
  IsoCount = 0
  IsoHidden = false
  IsoVisible = false
  LockPosition = false
  Perspective = false
  Rotation = 0
  RotationVector = (1,0,0)
  ScaleType = 2
  SeamHidden = false
  SeamVisible = true
  SmoothHidden = false
  SmoothVisible = true
  Source = -> [Cut001]
  Type = 5
  X = 0
  XDirection = (0,0,-1)
  Y = 67.1947
FEATURE [TechDraw::DrawProjGroupItem] ProjItem004  label="Top"
  CoarseView = false
  Direction = (-1,0,0)
  Focus = 100
  HardHidden = false
  IsoCount = 0
  IsoHidden = false
  IsoVisible = false
  LockPosition = false
  Perspective = false
  Rotation = 0
  RotationVector = (1,0,0)
  ScaleType = 2
  SeamHidden = false
  SeamVisible = true
  SmoothHidden = false
  SmoothVisible = true
  Source = -> [Cut001]
  Type = 4
  X = 0
  XDirection = (0,0,-1)
  Y = -67.7571
FEATURE [TechDraw::DrawProjGroup] ProjGroup
  Anchor = -> ProjItem
  AutoDistribute = true
  LockPosition = false
  ProjectionType = 0
  Rotation = 0
  ScaleType = 0
  Source = -> [Cut001]
  Views = -> [ProjItem,ProjItem001,ProjItem002,ProjItem003,ProjItem004]
  X = 92.8803
  Y = 118.668
  spacingX = 15
  spacingY = 15
FEATURE [TechDraw::DrawViewDimension] Dimension
  AngleOverride = false
  Arbitrary = false
  ArbitraryTolerances = false
  EqualTolerance = true
  ExtensionAngle = 0
  FormatSpec = %.2w
  FormatSpecOverTolerance = %+.2w
  FormatSpecUnderTolerance = %+.2w
  Inverted = false
  LineAngle = 0
  LockPosition = false
  MeasureType = 1
  OverTolerance = 0
  References2D = -> [ProjItem002]
  Rotation = 0
  ScaleType = 0
  TheoreticalExact = false
  Type = 0
  UnderTolerance = 0
  X = 18.1793
  Y = 2.5
FEATURE [TechDraw::DrawViewDimension] Dimension001
  AngleOverride = false
  Arbitrary = false
  ArbitraryTolerances = false
  EqualTolerance = true
  ExtensionAngle = 0
  FormatSpec = %.2w
  FormatSpecOverTolerance = %+.2w
  FormatSpecUnderTolerance = %+.2w
  Inverted = false
  LineAngle = 0
  LockPosition = false
  MeasureType = 1
  OverTolerance = 0
  References2D = -> [ProjItem002]
  Rotation = 0
  ScaleType = 0
  TheoreticalExact = false
  Type = 0
  UnderTolerance = 0
  X = -0.392399
  Y = 61.2636
FEATURE [TechDraw::DrawViewDimension] Dimension002
  AngleOverride = false
  Arbitrary = false
  ArbitraryTolerances = false
  EqualTolerance = true
  ExtensionAngle = 0
  FormatSpec = %.2w
  FormatSpecOverTolerance = %+.2w
  FormatSpecUnderTolerance = %+.2w
  Inverted = false
  LineAngle = 0
  LockPosition = false
  MeasureType = 1
  OverTolerance = 0
  References2D = -> [ProjItem]
  Rotation = 0
  ScaleType = 0
  TheoreticalExact = false
  Type = 0
  UnderTolerance = 0
  X = 44.1743
  Y = -37.5
FEATURE [TechDraw::DrawViewDimension] Dimension003
  AngleOverride = false
  Arbitrary = false
  ArbitraryTolerances = false
  EqualTolerance = true
  ExtensionAngle = 0
  FormatSpec = %.2w
  FormatSpecOverTolerance = %+.2w
  FormatSpecUnderTolerance = %+.2w
  Inverted = false
  LineAngle = 0
  LockPosition = false
  MeasureType = 1
  OverTolerance = 0
  References2D = -> [ProjItem]
  Rotation = 0
  ScaleType = 0
  TheoreticalExact = false
  Type = 0
  UnderTolerance = 0
  X = 40.3767
  Y = -18.0345
FEATURE [TechDraw::DrawViewDimension] Dimension004
  AngleOverride = false
  Arbitrary = false
  ArbitraryTolerances = false
  EqualTolerance = true
  ExtensionAngle = 0
  FormatSpec = %.2w
  FormatSpecOverTolerance = %+.2w
  FormatSpecUnderTolerance = %+.2w
  Inverted = false
  LineAngle = 0
  LockPosition = false
  MeasureType = 1
  OverTolerance = 0
  References2D = -> [ProjItem004]
  Rotation = 0
  ScaleType = 0
  TheoreticalExact = false
  Type = 0
  UnderTolerance = 0
  X = -0.2616
  Y = -12.0568
FEATURE [TechDraw::DrawViewDimension] Dimension005
  AngleOverride = false
  Arbitrary = false
  ArbitraryTolerances = false
  EqualTolerance = true
  ExtensionAngle = 0
  FormatSpec = ⌀%.2w (4x)
  FormatSpecOverTolerance = %+.2w
  FormatSpecUnderTolerance = %+.2w
  Inverted = false
  LineAngle = 0
  LockPosition = false
  MeasureType = 1
  OverTolerance = 0
  References2D = -> [ProjItem]
  Rotation = 0
  ScaleType = 0
  TheoreticalExact = false
  Type = 5
  UnderTolerance = 0
  X = -14.8914
  Y = -16.9228
FEATURE [TechDraw::DrawViewDimension] Dimension006
  AngleOverride = false
  Arbitrary = false
  ArbitraryTolerances = false
  EqualTolerance = true
  ExtensionAngle = 0
  FormatSpec = %.2w
  FormatSpecOverTolerance = %+.2w
  FormatSpecUnderTolerance = %+.2w
  Inverted = false
  LineAngle = 0
  LockPosition = false
  MeasureType = 1
  OverTolerance = 0
  References2D = -> [ProjItem002]
  Rotation = 0
  ScaleType = 0
  TheoreticalExact = false
  Type = 0
  UnderTolerance = 0
  X = -9.2228
  Y = -18.7975
FEATURE [TechDraw::DrawViewDimension] Dimension007
  AngleOverride = false
  Arbitrary = false
  ArbitraryTolerances = false
  EqualTolerance = true
  ExtensionAngle = 0
  FormatSpec = %.2w
  FormatSpecOverTolerance = %+.2w
  FormatSpecUnderTolerance = %+.2w
  Inverted = false
  LineAngle = 0
  LockPosition = false
  MeasureType = 1
  OverTolerance = 0
  References2D = -> [ProjItem002]
  Rotation = 0
  ScaleType = 0
  TheoreticalExact = false
  Type = 0
  UnderTolerance = 0
  X = -11.0338
  Y = -36.7557
FEATURE [TechDraw::DrawViewDimension] Dimension008
  AngleOverride = false
  Arbitrary = false
  ArbitraryTolerances = false
  EqualTolerance = true
  ExtensionAngle = 0
  FormatSpec = ⌀%.2w
  FormatSpecOverTolerance = %+.2w
  FormatSpecUnderTolerance = %+.2w
  Inverted = false
  LineAngle = 0
  LockPosition = false
  MeasureType = 1
  OverTolerance = 0
  References2D = -> [ProjItem002]
  Rotation = 0
  ScaleType = 0
  TheoreticalExact = false
  Type = 5
  UnderTolerance = 0
  X = 12.2078
  Y = 35.5126
FEATURE [TechDraw::DrawPage] Page
  KeepUpdated = true
  NextBalloonIndex = 1
  ProjectionType = 0
  Template = -> Template
  Views = -> [ProjGroup,Dimension,Dimension001,Dimension002,Dimension003,Dimension004,Dimension005,Dimension006,Dimension007,Dimension008]
---- part MechanicalCF35Mount003.FCStd = doc fcstd_7e9f5c0df34d ----
FCSTD DOCUMENT  (FreeCAD 0.20R29603 (Git))
Label: MechanicalCF35Mount003
License: All rights reserved
LicenseURL: http://en.wikipedia.org/wiki/All_rights_reserved
objects: Part::Cylinder×14, TechDraw::DrawViewDimension×13, Part::Compound×10, TechDraw::DrawProjGroupItem×4, Part::Box×3, Part::Cut×2, Part::FeaturePython×1, Part::Feature×1, TechDraw::DrawSVGTemplate×1, TechDraw::DrawProjGroup×1, TechDraw::DrawPage×1
note: 31 computed .brp shape members not serialized (recipe doc carries the construction recipe); baked Part::Feature solids carry a one-line shape summary decoded from their .brp

FEATURE [Part::Box] Box  label="Würfel"
  AttacherType = Attacher::AttachEngine3D
  Height = 1.8
  Length = 103.6
  Placement = pos=(-51.8,-305,50) rot=(0,0,1;0rad)
  Width = 317.7
FEATURE [Part::Box] Box001  label="Würfel001"
  AttacherType = Attacher::AttachEngine3D
  Height = 1.8
  Length = 103.6
  Placement = pos=(-51.8,-305,50) rot=(0,1,0;1.5708rad)
  Width = 317.7
FEATURE [Part::Box] Box002  label="Würfel002"
  AttacherType = Attacher::AttachEngine3D
  Height = 1.8
  Length = 103.6
  Placement = pos=(50,-305,50) rot=(0,1,0;1.5708rad)
  Width = 317.7
FEATURE [Part::Compound] Compound006
  Links = -> [Box,Box001,Box002]
FEATURE [Part::Cylinder] Cylinder004  label="Zylinder004"
  Angle = 360
  AttacherType = Attacher::AttachEngine3D
  FirstAngle = 0
  Height = 200
  Placement = pos=(30,6.35,-100) rot=(0,0,1;0rad)
  Radius = 3.3
  SecondAngle = 0
FEATURE [Part::Cylinder] Cylinder005  label="Zylinder005"
  Angle = 360
  AttacherType = Attacher::AttachEngine3D
  FirstAngle = 0
  Height = 200
  Placement = pos=(-30,6.35,-100) rot=(0,0,1;0rad)
  Radius = 3.3
  SecondAngle = 0
FEATURE [Part::Cylinder] Cylinder006  label="Zylinder006"
  Angle = 360
  AttacherType = Attacher::AttachEngine3D
  FirstAngle = 0
  Height = 200
  Placement = pos=(-30,6.35,-100) rot=(0,0,1;0rad)
  Radius = 3.3
  SecondAngle = 0
FEATURE [Part::Cylinder] Cylinder007  label="Zylinder007"
  Angle = 360
  AttacherType = Attacher::AttachEngine3D
  FirstAngle = 0
  Height = 200
  Placement = pos=(30,6.35,-100) rot=(0,0,1;0rad)
  Radius = 3.3
  SecondAngle = 0
FEATURE [Part::Compound] Compound004
  Links = -> [Cylinder006,Cylinder007]
  Placement = pos=(0,0,0) rot=(0,1,0;1.5708rad)
FEATURE [Part::Compound] Compound005
  Links = -> [Cylinder004,Cylinder005,Compound004]
FEATURE [Part::Cylinder] Cylinder008  label="Zylinder008"
  Angle = 360
  AttacherType = Attacher::AttachEngine3D
  FirstAngle = 0
  Height = 200
  Placement = pos=(0,6.35,-100) rot=(0,0,1;0rad)
  Radius = 3.3
  SecondAngle = 0
FEATURE [Part::Cylinder] Cylinder009  label="Zylinder009"
  Angle = 360
  AttacherType = Attacher::AttachEngine3D
  FirstAngle = 0
  Height = 200
  Placement = pos=(0,6.35,-100) rot=(0,0,1;0rad)
  Radius = 3.3
  SecondAngle = 0
FEATURE [Part::Compound] Compound007
  Links = -> [Cylinder009]
  Placement = pos=(0,0,0) rot=(0,1,0;1.5708rad)
FEATURE [Part::Compound] Compound008
  Links = -> [Compound005,Cylinder008,Compound007]
FEATURE [Part::Cut] Cut
  Base = -> Compound006
  Tool = -> Compound008
FEATURE [Part::FeaturePython] Connect  # WARN: FeaturePython — macro-defined, semantics opaque (R4)
  Objects = -> [Cut]
  Tolerance = 0
FEATURE [Part::Cylinder] Cylinder  label="Zylinder"
  Angle = 360
  AttacherType = Attacher::AttachEngine3D
  FirstAngle = 0
  Height = 20
  Placement = pos=(30,2,40) rot=(0,0,1;0rad)
  Radius = 1.2
  SecondAngle = 0
FEATURE [Part::Cylinder] Cylinder015  label="Zylinder015"
  Angle = 360
  AttacherType = Attacher::AttachEngine3D
  FirstAngle = 0
  Height = 20
  Placement = pos=(-30,2,40) rot=(0,0,1;0rad)
  Radius = 1.2
  SecondAngle = 0
FEATURE [Part::Compound] Compound
  Links = -> [Cylinder,Cylinder015]
FEATURE [Part::Cylinder] Cylinder016  label="Zylinder016"
  Angle = 360
  AttacherType = Attacher::AttachEngine3D
  FirstAngle = 0
  Height = 20
  Placement = pos=(30,2,40) rot=(0,0,1;0rad)
  Radius = 1.2
  SecondAngle = 0
FEATURE [Part::Cylinder] Cylinder017  label="Zylinder017"
  Angle = 360
  AttacherType = Attacher::AttachEngine3D
  FirstAngle = 0
  Height = 20
  Placement = pos=(-30,2,40) rot=(0,0,1;0rad)
  Radius = 1.2
  SecondAngle = 0
FEATURE [Part::Compound] Compound015
  Links = -> [Cylinder016,Cylinder017]
  Placement = pos=(0,0,0) rot=(0,1,0;1.5708rad)
FEATURE [Part::Cylinder] Cylinder018  label="Zylinder018"
  Angle = 360
  AttacherType = Attacher::AttachEngine3D
  FirstAngle = 0
  Height = 20
  Placement = pos=(30,2,40) rot=(0,0,1;0rad)
  Radius = 1.2
  SecondAngle = 0
FEATURE [Part::Cylinder] Cylinder019  label="Zylinder019"
  Angle = 360
  AttacherType = Attacher::AttachEngine3D
  FirstAngle = 0
  Height = 20
  Placement = pos=(-30,2,40) rot=(0,0,1;0rad)
  Radius = 1.2
  SecondAngle = 0
FEATURE [Part::Compound] Compound016
  Links = -> [Cylinder018,Cylinder019]
  Placement = pos=(0,0,0) rot=(0,1,0;3.14159rad)
FEATURE [Part::Cylinder] Cylinder020  label="Zylinder020"
  Angle = 360
  AttacherType = Attacher::AttachEngine3D
  FirstAngle = 0
  Height = 20
  Placement = pos=(30,2,40) rot=(0,0,1;0rad)
  Radius = 1.2
  SecondAngle = 0
FEATURE [Part::Cylinder] Cylinder021  label="Zylinder021"
  Angle = 360
  AttacherType = Attacher::AttachEngine3D
  FirstAngle = 0
  Height = 20
  Placement = pos=(-30,2,40) rot=(0,0,1;0rad)
  Radius = 1.2
  SecondAngle = 0
FEATURE [Part::Compound] Compound017
  Links = -> [Cylinder020,Cylinder021]
  Placement = pos=(0,0,0) rot=(0,-1,0;1.5708rad)
FEATURE [Part::Compound] Compound018  label="M2Corehole"
  Links = -> [Compound017,Compound,Compound015,Compound016]
  Placement = pos=(0,-302,0) rot=(0,0,1;0rad)
FEATURE [Part::Cut] Cut001
  Base = -> Connect
  Tool = -> Compound018
FEATURE [Part::Feature] Cut001_solid  label="Cut001 (Solid)"
  shape: bbox 103.6 x 317.7 x 105.4 mm, 31 faces (baked)
FEATURE [TechDraw::DrawSVGTemplate] Template
  EditableTexts = Designed_by_Name=Thomas Spielauer; FC-Date=2023-07-05; FC-SC=mm; FC-SH=01; FC-Title=CF40 electronics housing; Subtitle=Cover sheet
  Height = 210
  Orientation = 1
  Width = 297
FEATURE [TechDraw::DrawProjGroupItem] ProjItem  label="Front"
  CoarseView = false
  Direction = (0,0,1)
  Focus = 100
  HardHidden = false
  IsoCount = 0
  IsoHidden = false
  IsoVisible = false
  LockPosition = true
  Perspective = false
  Rotation = 0
  RotationVector = (1,0,0)
  Scale = 0.333333
  ScaleType = 2
  SeamHidden = false
  SeamVisible = true
  SmoothHidden = false
  SmoothVisible = true
  Source = -> [Cut001]
  Type = 0
  X = 0
  XDirection = (1,0,0)
  Y = 0
FEATURE [TechDraw::DrawProjGroupItem] ProjItem001  label="Right"
  CoarseView = false
  Direction = (1,0,1e-16)
  Focus = 100
  HardHidden = false
  IsoCount = 0
  IsoHidden = false
  IsoVisible = false
  LockPosition = false
  Perspective = false
  Rotation = 0
  RotationVector = (1,0,0)
  Scale = 0.333333
  ScaleType = 2
  SeamHidden = false
  SeamVisible = true
  SmoothHidden = false
  SmoothVisible = true
  Source = -> [Cut001]
  Type = 2
  X = -35.1333
  XDirection = (1e-16,0,-1)
  Y = 0
FEATURE [TechDraw::DrawProjGroupItem] ProjItem002  label="Left"
  CoarseView = false
  Direction = (-1,0,1e-16)
  Focus = 100
  HardHidden = false
  IsoCount = 0
  IsoHidden = false
  IsoVisible = false
  LockPosition = false
  Perspective = false
  Rotation = 0
  RotationVector = (1,0,0)
  Scale = 0.333333
  ScaleType = 2
  SeamHidden = false
  SeamVisible = true
  SmoothHidden = false
  SmoothVisible = true
  Source = -> [Cut001]
  Type = 1
  X = 35.1333
  XDirection = (1e-16,0,1)
  Y = 0
FEATURE [TechDraw::DrawProjGroupItem] ProjItem003  label="Bottom"
  CoarseView = false
  Direction = (0,-1,0)
  Focus = 100
  HardHidden = false
  IsoCount = 0
  IsoHidden = false
  IsoVisible = false
  LockPosition = false
  Perspective = false
  Rotation = 0
  RotationVector = (1,0,0)
  ScaleType = 2
  SeamHidden = false
  SeamVisible = true
  SmoothHidden = false
  SmoothVisible = true
  Source = -> [Cut001]
  Type = 5
  X = 0
  XDirection = (1,0,0)
  Y = -90.9455
FEATURE [TechDraw::DrawProjGroup] ProjGroup
  Anchor = -> ProjItem
  AutoDistribute = true
  LockPosition = false
  ProjectionType = 0
  Rotation = 0
  Scale = 0.333333
  ScaleType = 2
  Source = -> [Cut001]
  Views = -> [ProjItem,ProjItem001,ProjItem002,ProjItem003]
  X = 86.7905
  Y = 137.808
  spacingX = 0
  spacingY = 0
FEATURE [TechDraw::DrawViewDimension] Dimension
  AngleOverride = false
  Arbitrary = false
  ArbitraryTolerances = false
  EqualTolerance = true
  ExtensionAngle = 0
  FormatSpec = %.2w
  FormatSpecOverTolerance = %+.2w
  FormatSpecUnderTolerance = %+.2w
  Inverted = false
  LineAngle = 0
  LockPosition = false
  MeasureType = 1
  OverTolerance = 0
  References2D = -> [ProjItem003]
  Rotation = 0
  ScaleType = 0
  TheoreticalExact = false
  Type = 0
  UnderTolerance = 0
  X = 21.5083
  Y = -23.6998
FEATURE [TechDraw::DrawViewDimension] Dimension001
  AngleOverride = false
  Arbitrary = false
  ArbitraryTolerances = false
  EqualTolerance = true
  ExtensionAngle = 0
  FormatSpec = %.2w
  FormatSpecOverTolerance = %+.2w
  FormatSpecUnderTolerance = %+.2w
  Inverted = false
  LineAngle = 0
  LockPosition = false
  MeasureType = 1
  OverTolerance = 0
  References2D = -> [ProjItem003]
  Rotation = 0
  ScaleType = 0
  TheoreticalExact = false
  Type = 0
  UnderTolerance = 0
  X = 0.573136
  Y = 27.3701
FEATURE [TechDraw::DrawViewDimension] Dimension002
  AngleOverride = false
  Arbitrary = false
  ArbitraryTolerances = false
  EqualTolerance = true
  ExtensionAngle = 0
  FormatSpec = %.2w
  FormatSpecOverTolerance = %+.2w
  FormatSpecUnderTolerance = %+.2w
  Inverted = false
  LineAngle = 0
  LockPosition = false
  MeasureType = 1
  OverTolerance = 0
  References2D = -> [ProjItem003]
  Rotation = 0
  ScaleType = 0
  TheoreticalExact = false
  Type = 0
  UnderTolerance = 0
  X = -22.7166
  Y = 2.30499
FEATURE [TechDraw::DrawViewDimension] Dimension003
  AngleOverride = false
  Arbitrary = false
  ArbitraryTolerances = false
  EqualTolerance = true
  ExtensionAngle = 0
  FormatSpec = %.2w
  FormatSpecOverTolerance = %+.2w
  FormatSpecUnderTolerance = %+.2w
  Inverted = false
  LineAngle = 0
  LockPosition = false
  MeasureType = 1
  OverTolerance = 0
  References2D = -> [ProjItem002]
  Rotation = 0
  ScaleType = 0
  TheoreticalExact = false
  Type = 0
  UnderTolerance = 0
  X = 31.3231
  Y = 1.75722
FEATURE [TechDraw::DrawViewDimension] Dimension004
  AngleOverride = false
  Arbitrary = false
  ArbitraryTolerances = false
  EqualTolerance = true
  ExtensionAngle = 0
  FormatSpec = %.2w
  FormatSpecOverTolerance = %+.2w
  FormatSpecUnderTolerance = %+.2w
  Inverted = false
  LineAngle = 0
  LockPosition = false
  MeasureType = 1
  OverTolerance = 0
  References2D = -> [ProjItem002]
  Rotation = 0
  ScaleType = 0
  TheoreticalExact = false
  Type = 0
  UnderTolerance = 0
  X = -0.30401
  Y = 61.5395
FEATURE [TechDraw::DrawViewDimension] Dimension005
  AngleOverride = false
  Arbitrary = false
  ArbitraryTolerances = false
  EqualTolerance = true
  ExtensionAngle = 0
  FormatSpec = %.2w
  FormatSpecOverTolerance = %+.2w
  FormatSpecUnderTolerance = %+.2w
  Inverted = false
  LineAngle = 0
  LockPosition = false
  MeasureType = 1
  OverTolerance = 0
  References2D = -> [ProjItem]
  Rotation = 0
  ScaleType = 0
  TheoreticalExact = false
  Type = 0
  UnderTolerance = 0
  X = 0.35821
  Y = 61.5395
FEATURE [TechDraw::DrawViewDimension] Dimension006
  AngleOverride = false
  Arbitrary = false
  ArbitraryTolerances = false
  EqualTolerance = true
  ExtensionAngle = 0
  FormatSpec = %.2w
  FormatSpecOverTolerance = %+.2w
  FormatSpecUnderTolerance = %+.2w
  Inverted = false
  LineAngle = 0
  LockPosition = false
  MeasureType = 1
  OverTolerance = 0
  References2D = -> [ProjItem001]
  Rotation = 0
  ScaleType = 0
  TheoreticalExact = false
  Type = 0
  UnderTolerance = 0
  X = 0.901027
  Y = 61.7783
FEATURE [TechDraw::DrawViewDimension] Dimension007
  AngleOverride = false
  Arbitrary = false
  ArbitraryTolerances = false
  EqualTolerance = true
  ExtensionAngle = 0
  FormatSpec = %.2w
  FormatSpecOverTolerance = %+.2w
  FormatSpecUnderTolerance = %+.2w
  Inverted = false
  LineAngle = 0
  LockPosition = false
  MeasureType = 1
  OverTolerance = 0
  References2D = -> [ProjItem002]
  Rotation = 0
  ScaleType = 0
  TheoreticalExact = false
  Type = 0
  UnderTolerance = 0
  X = 13.1295
  Y = -40.785
FEATURE [TechDraw::DrawViewDimension] Dimension008
  AngleOverride = false
  Arbitrary = false
  ArbitraryTolerances = false
  EqualTolerance = true
  ExtensionAngle = 0
  FormatSpec = %.2w
  FormatSpecOverTolerance = %+.2w
  FormatSpecUnderTolerance = %+.2w
  Inverted = false
  LineAngle = 0
  LockPosition = false
  MeasureType = 1
  OverTolerance = 0
  References2D = -> [ProjItem002]
  Rotation = 0
  ScaleType = 0
  TheoreticalExact = false
  Type = 0
  UnderTolerance = 0
  X = 4.06525
  Y = -54.1819
FEATURE [TechDraw::DrawViewDimension] Dimension009
  AngleOverride = false
  Arbitrary = false
  ArbitraryTolerances = false
  EqualTolerance = true
  ExtensionAngle = 0
  FormatSpec = ⌀%.2w (6x)
  FormatSpecOverTolerance = %+.2w
  FormatSpecUnderTolerance = %+.2w
  Inverted = false
  LineAngle = 0
  LockPosition = false
  MeasureType = 1
  OverTolerance = 0
  References2D = -> [ProjItem]
  Rotation = 0
  ScaleType = 0
  TheoreticalExact = false
  Type = 5
  UnderTolerance = 0
  X = 4.91331
  Y = -37.9481
FEATURE [TechDraw::DrawViewDimension] Dimension010
  AngleOverride = false
  Arbitrary = false
  ArbitraryTolerances = false
  EqualTolerance = true
  ExtensionAngle = 0
  FormatSpec = %.2w
  FormatSpecOverTolerance = %+.2w
  FormatSpecUnderTolerance = %+.2w
  Inverted = false
  LineAngle = 0
  LockPosition = false
  MeasureType = 1
  OverTolerance = 0
  References2D = -> [ProjItem002]
  Rotation = 0
  ScaleType = 0
  TheoreticalExact = false
  Type = 0
  UnderTolerance = 0
  X = 13.3665
  Y = 47.2497
FEATURE [TechDraw::DrawViewDimension] Dimension011
  AngleOverride = false
  Arbitrary = false
  ArbitraryTolerances = false
  EqualTolerance = true
  ExtensionAngle = 0
  FormatSpec = %.2w
  FormatSpecOverTolerance = %+.2w
  FormatSpecUnderTolerance = %+.2w
  Inverted = false
  LineAngle = 0
  LockPosition = false
  MeasureType = 1
  OverTolerance = 0
  References2D = -> [ProjItem002]
  Rotation = 0
  ScaleType = 0
  TheoreticalExact = false
  Type = 0
  UnderTolerance = 0
  X = 13.4962
  Y = 39.3495
FEATURE [TechDraw::DrawViewDimension] Dimension012
  AngleOverride = false
  Arbitrary = false
  ArbitraryTolerances = false
  EqualTolerance = true
  ExtensionAngle = 0
  FormatSpec = ⌀%.2w (9x)
  FormatSpecOverTolerance = %+.2w
  FormatSpecUnderTolerance = %+.2w
  Inverted = false
  LineAngle = 0
  LockPosition = false
  MeasureType = 1
  OverTolerance = 0
  References2D = -> [ProjItem]
  Rotation = 0
  ScaleType = 0
  TheoreticalExact = false
  Type = 5
  UnderTolerance = 0
  X = 6.43535
  Y = 37.659
FEATURE [TechDraw::DrawPage] Page
  KeepUpdated = true
  NextBalloonIndex = 1
  ProjectionType = 0
  Template = -> Template
  Views = -> [ProjGroup,Dimension,Dimension001,Dimension002,Dimension003,Dimension004,Dimension005,Dimension006,Dimension007,Dimension008,Dimension009,Dimension010,Dimension011,Dimension012]
---- part MechanicalCF35Mount004.FCStd = doc fcstd_a3e4b36090e4 ----
FCSTD DOCUMENT  (FreeCAD 0.20R29603 (Git))
Label: MechanicalCF35Mount004
License: All rights reserved
LicenseURL: http://en.wikipedia.org/wiki/All_rights_reserved
objects: Part::Cylinder×14, Part::Compound×10, TechDraw::DrawViewDimension×8, TechDraw::DrawProjGroupItem×2, Part::Box×1, Part::Cut×1, Part::Feature×1, TechDraw::DrawSVGTemplate×1, TechDraw::DrawProjGroup×1, TechDraw::DrawPage×1
note: 27 computed .brp shape members not serialized (recipe doc carries the construction recipe); baked Part::Feature solids carry a one-line shape summary decoded from their .brp

FEATURE [Part::Box] Box  label="Würfel"
  AttacherType = Attacher::AttachEngine3D
  Height = 1.8
  Length = 100
  Placement = pos=(-50,-305,50) rot=(0,0,1;0rad)
  Width = 317.7
FEATURE [Part::Cylinder] Cylinder  label="Zylinder"
  Angle = 360
  AttacherType = Attacher::AttachEngine3D
  FirstAngle = 0
  Height = 20
  Placement = pos=(30,2,40) rot=(0,0,1;0rad)
  Radius = 1.2
  SecondAngle = 0
FEATURE [Part::Cylinder] Cylinder015  label="Zylinder015"
  Angle = 360
  AttacherType = Attacher::AttachEngine3D
  FirstAngle = 0
  Height = 20
  Placement = pos=(-30,2,40) rot=(0,0,1;0rad)
  Radius = 1.2
  SecondAngle = 0
FEATURE [Part::Compound] Compound
  Links = -> [Cylinder,Cylinder015]
FEATURE [Part::Cylinder] Cylinder016  label="Zylinder016"
  Angle = 360
  AttacherType = Attacher::AttachEngine3D
  FirstAngle = 0
  Height = 20
  Placement = pos=(30,2,40) rot=(0,0,1;0rad)
  Radius = 1.2
  SecondAngle = 0
FEATURE [Part::Cylinder] Cylinder017  label="Zylinder017"
  Angle = 360
  AttacherType = Attacher::AttachEngine3D
  FirstAngle = 0
  Height = 20
  Placement = pos=(-30,2,40) rot=(0,0,1;0rad)
  Radius = 1.2
  SecondAngle = 0
FEATURE [Part::Compound] Compound015
  Links = -> [Cylinder016,Cylinder017]
  Placement = pos=(0,0,0) rot=(0,1,0;1.5708rad)
FEATURE [Part::Cylinder] Cylinder018  label="Zylinder018"
  Angle = 360
  AttacherType = Attacher::AttachEngine3D
  FirstAngle = 0
  Height = 20
  Placement = pos=(30,2,40) rot=(0,0,1;0rad)
  Radius = 1.2
  SecondAngle = 0
FEATURE [Part::Cylinder] Cylinder019  label="Zylinder019"
  Angle = 360
  AttacherType = Attacher::AttachEngine3D
  FirstAngle = 0
  Height = 20
  Placement = pos=(-30,2,40) rot=(0,0,1;0rad)
  Radius = 1.2
  SecondAngle = 0
FEATURE [Part::Compound] Compound016
  Links = -> [Cylinder018,Cylinder019]
  Placement = pos=(0,0,0) rot=(0,1,0;3.14159rad)
FEATURE [Part::Cylinder] Cylinder020  label="Zylinder020"
  Angle = 360
  AttacherType = Attacher::AttachEngine3D
  FirstAngle = 0
  Height = 20
  Placement = pos=(30,2,40) rot=(0,0,1;0rad)
  Radius = 1.2
  SecondAngle = 0
FEATURE [Part::Cylinder] Cylinder021  label="Zylinder021"
  Angle = 360
  AttacherType = Attacher::AttachEngine3D
  FirstAngle = 0
  Height = 20
  Placement = pos=(-30,2,40) rot=(0,0,1;0rad)
  Radius = 1.2
  SecondAngle = 0
FEATURE [Part::Compound] Compound017
  Links = -> [Cylinder020,Cylinder021]
  Placement = pos=(0,0,0) rot=(0,-1,0;1.5708rad)
FEATURE [Part::Compound] Compound018  label="M2Corehole"
  Links = -> [Compound017,Compound,Compound015,Compound016]
  Placement = pos=(0,-302,0) rot=(0,0,1;0rad)
FEATURE [Part::Cylinder] Cylinder004  label="Zylinder004"
  Angle = 360
  AttacherType = Attacher::AttachEngine3D
  FirstAngle = 0
  Height = 200
  Placement = pos=(30,6.35,-100) rot=(0,0,1;0rad)
  Radius = 3.3
  SecondAngle = 0
FEATURE [Part::Cylinder] Cylinder005  label="Zylinder005"
  Angle = 360
  AttacherType = Attacher::AttachEngine3D
  FirstAngle = 0
  Height = 200
  Placement = pos=(-30,6.35,-100) rot=(0,0,1;0rad)
  Radius = 3.3
  SecondAngle = 0
FEATURE [Part::Cylinder] Cylinder006  label="Zylinder006"
  Angle = 360
  AttacherType = Attacher::AttachEngine3D
  FirstAngle = 0
  Height = 200
  Placement = pos=(-30,6.35,-100) rot=(0,0,1;0rad)
  Radius = 3.3
  SecondAngle = 0
FEATURE [Part::Cylinder] Cylinder007  label="Zylinder007"
  Angle = 360
  AttacherType = Attacher::AttachEngine3D
  FirstAngle = 0
  Height = 200
  Placement = pos=(30,6.35,-100) rot=(0,0,1;0rad)
  Radius = 3.3
  SecondAngle = 0
FEATURE [Part::Compound] Compound004
  Links = -> [Cylinder006,Cylinder007]
  Placement = pos=(0,0,0) rot=(0,1,0;1.5708rad)
FEATURE [Part::Compound] Compound005
  Links = -> [Cylinder004,Cylinder005,Compound004]
FEATURE [Part::Cylinder] Cylinder008  label="Zylinder008"
  Angle = 360
  AttacherType = Attacher::AttachEngine3D
  FirstAngle = 0
  Height = 200
  Placement = pos=(0,6.35,-100) rot=(0,0,1;0rad)
  Radius = 3.3
  SecondAngle = 0
FEATURE [Part::Cylinder] Cylinder009  label="Zylinder009"
  Angle = 360
  AttacherType = Attacher::AttachEngine3D
  FirstAngle = 0
  Height = 200
  Placement = pos=(0,6.35,-100) rot=(0,0,1;0rad)
  Radius = 3.3
  SecondAngle = 0
FEATURE [Part::Compound] Compound007
  Links = -> [Cylinder009]
  Placement = pos=(0,0,0) rot=(0,1,0;1.5708rad)
FEATURE [Part::Compound] Compound008
  Links = -> [Compound005,Cylinder008,Compound007]
FEATURE [Part::Compound] Compound019
  Links = -> [Compound018,Compound008]
FEATURE [Part::Cut] Cut
  Base = -> Box
  Tool = -> Compound019
FEATURE [Part::Feature] Cut_solid  label="Cut (Solid)"
  shape: bbox 100 x 317.7 x 1.8 mm, 11 faces (baked)
FEATURE [TechDraw::DrawSVGTemplate] Template
  EditableTexts = Designed_by_Name=Thoams Spielauer; FC-Date=2023-07-05; FC-SC=mm; FC-SH=01; FC-Title=CF40 electronics housing; Subtitle=Bottom sheet
  Height = 210
  Orientation = 1
  Width = 297
FEATURE [TechDraw::DrawProjGroupItem] ProjItem  label="Front"
  CoarseView = false
  Direction = (0,0,1)
  Focus = 100
  HardHidden = false
  IsoCount = 0
  IsoHidden = false
  IsoVisible = false
  LockPosition = true
  Perspective = false
  Rotation = 0
  RotationVector = (1,0,0)
  Scale = 0.333333
  ScaleType = 2
  SeamHidden = false
  SeamVisible = true
  SmoothHidden = false
  SmoothVisible = true
  Source = -> [Cut_solid]
  Type = 0
  X = 0
  XDirection = (1,0,0)
  Y = 0
FEATURE [TechDraw::DrawProjGroupItem] ProjItem001  label="Left"
  CoarseView = false
  Direction = (-1,0,1e-16)
  Focus = 100
  HardHidden = false
  IsoCount = 0
  IsoHidden = false
  IsoVisible = false
  LockPosition = false
  Perspective = false
  Rotation = 0
  RotationVector = (1,0,0)
  ScaleType = 2
  SeamHidden = false
  SeamVisible = true
  SmoothHidden = false
  SmoothVisible = true
  Source = -> [Cut_solid]
  Type = 1
  X = 48.3333
  XDirection = (1e-16,0,1)
  Y = 0
FEATURE [TechDraw::DrawProjGroup] ProjGroup
  Anchor = -> ProjItem
  AutoDistribute = true
  LockPosition = false
  ProjectionType = 0
  Rotation = 0
  Scale = 0.333333
  ScaleType = 2
  Source = -> [Cut_solid]
  Views = -> [ProjItem,ProjItem001]
  X = 87.4123
  Y = 128.335
  spacingX = 15
  spacingY = 15
FEATURE [TechDraw::DrawViewDimension] Dimension
  AngleOverride = false
  Arbitrary = false
  ArbitraryTolerances = false
  EqualTolerance = true
  ExtensionAngle = 0
  FormatSpec = %.2w
  FormatSpecOverTolerance = %+.2w
  FormatSpecUnderTolerance = %+.2w
  Inverted = false
  LineAngle = 0
  LockPosition = false
  MeasureType = 1
  OverTolerance = 0
  References2D = -> [ProjItem]
  Rotation = 0
  ScaleType = 0
  TheoreticalExact = false
  Type = 0
  UnderTolerance = 0
  X = -33.2555
  Y = 1.26203
FEATURE [TechDraw::DrawViewDimension] Dimension001
  AngleOverride = false
  Arbitrary = false
  ArbitraryTolerances = false
  EqualTolerance = true
  ExtensionAngle = 0
  FormatSpec = %.2w
  FormatSpecOverTolerance = %+.2w
  FormatSpecUnderTolerance = %+.2w
  Inverted = false
  LineAngle = 0
  LockPosition = false
  MeasureType = 1
  OverTolerance = 0
  References2D = -> [ProjItem]
  Rotation = 0
  ScaleType = 0
  TheoreticalExact = false
  Type = 0
  UnderTolerance = 0
  X = -1.23797
  Y = -66.7912
FEATURE [TechDraw::DrawViewDimension] Dimension002
  AngleOverride = false
  Arbitrary = false
  ArbitraryTolerances = false
  EqualTolerance = true
  ExtensionAngle = 0
  FormatSpec = %.2w
  FormatSpecOverTolerance = %+.2w
  FormatSpecUnderTolerance = %+.2w
  Inverted = false
  LineAngle = 0
  LockPosition = false
  MeasureType = 1
  OverTolerance = 0
  References2D = -> [ProjItem001]
  Rotation = 0
  ScaleType = 0
  TheoreticalExact = false
  Type = 0
  UnderTolerance = 0
  X = 0.102835
  Y = 63.4252
FEATURE [TechDraw::DrawViewDimension] Dimension003
  AngleOverride = false
  Arbitrary = false
  ArbitraryTolerances = false
  EqualTolerance = true
  ExtensionAngle = 0
  FormatSpec = %.2w
  FormatSpecOverTolerance = %+.2w
  FormatSpecUnderTolerance = %+.2w
  Inverted = false
  LineAngle = 0
  LockPosition = false
  MeasureType = 1
  OverTolerance = 0
  References2D = -> [ProjItem]
  Rotation = 0
  ScaleType = 0
  TheoreticalExact = false
  Type = 0
  UnderTolerance = 0
  X = 7.70254
  Y = 64.3208
FEATURE [TechDraw::DrawViewDimension] Dimension004
  AngleOverride = false
  Arbitrary = false
  ArbitraryTolerances = false
  EqualTolerance = true
  ExtensionAngle = 0
  FormatSpec = %.2w
  FormatSpecOverTolerance = %+.2w
  FormatSpecUnderTolerance = %+.2w
  Inverted = false
  LineAngle = 0
  LockPosition = false
  MeasureType = 1
  OverTolerance = 0
  References2D = -> [ProjItem]
  Rotation = 0
  ScaleType = 0
  TheoreticalExact = false
  Type = 0
  UnderTolerance = 0
  X = -12.2736
  Y = 64.3062
FEATURE [TechDraw::DrawViewDimension] Dimension005
  AngleOverride = false
  Arbitrary = false
  ArbitraryTolerances = false
  EqualTolerance = true
  ExtensionAngle = 0
  FormatSpec = ⌀%.2w (3x)
  FormatSpecOverTolerance = %+.2w
  FormatSpecUnderTolerance = %+.2w
  Inverted = false
  LineAngle = 0
  LockPosition = false
  MeasureType = 1
  OverTolerance = 0
  References2D = -> [ProjItem]
  Rotation = 0
  ScaleType = 0
  TheoreticalExact = false
  Type = 5
  UnderTolerance = 0
  X = 1.44604
  Y = 36.618
FEATURE [TechDraw::DrawViewDimension] Dimension006
  AngleOverride = false
  Arbitrary = false
  ArbitraryTolerances = false
  EqualTolerance = true
  ExtensionAngle = 0
  FormatSpec = %.2w
  FormatSpecOverTolerance = %+.2w
  FormatSpecUnderTolerance = %+.2w
  Inverted = false
  LineAngle = 0
  LockPosition = false
  MeasureType = 1
  OverTolerance = 0
  References2D = -> [ProjItem]
  Rotation = 0
  ScaleType = 0
  TheoreticalExact = false
  Type = 0
  UnderTolerance = 0
  X = 12.0421
  Y = -78.1672
FEATURE [TechDraw::DrawViewDimension] Dimension007
  AngleOverride = false
  Arbitrary = false
  ArbitraryTolerances = false
  EqualTolerance = true
  ExtensionAngle = 0
  FormatSpec = ⌀%.2w (2x)
  FormatSpecOverTolerance = %+.2w
  FormatSpecUnderTolerance = %+.2w
  Inverted = false
  LineAngle = 0
  LockPosition = false
  MeasureType = 1
  OverTolerance = 0
  References2D = -> [ProjItem]
  Rotation = 0
  ScaleType = 0
  TheoreticalExact = false
  Type = 5
  UnderTolerance = 0
  X = -9.25376
  Y = -35.5101
FEATURE [TechDraw::DrawPage] Page
  KeepUpdated = true
  NextBalloonIndex = 1
  ProjectionType = 0
  Template = -> Template
  Views = -> [ProjGroup,Dimension,Dimension001,Dimension002,Dimension003,Dimension004,Dimension005,Dimension006,Dimension007]
---- part MechanicalCF35Mount005.FCStd = doc fcstd_0632e6f44583 ----
FCSTD DOCUMENT  (FreeCAD 0.20R29603 (Git))
Label: MechanicalCF35Mount005
License: All rights reserved
LicenseURL: http://en.wikipedia.org/wiki/All_rights_reserved
objects: Part::Cylinder×6, Part::Compound×5, Part::Box×2, Part::Cut×2, Part::MultiCommon×1, Part::Feature×1
note: 17 computed .brp shape members not serialized (recipe doc carries the construction recipe); baked Part::Feature solids carry a one-line shape summary decoded from their .brp

FEATURE [Part::Cylinder] Cylinder  label="Zylinder"
  Angle = 360
  AttacherType = Attacher::AttachEngine3D
  FirstAngle = 0
  Height = 317.7
  Placement = pos=(-30,12.7,-30) rot=(1,0,0;1.5708rad)
  Radius = 3
  SecondAngle = 0
FEATURE [Part::Cylinder] Cylinder001  label="Zylinder001"
  Angle = 360
  AttacherType = Attacher::AttachEngine3D
  FirstAngle = 0
  Height = 317.7
  Placement = pos=(-30,12.7,-30) rot=(1,0,0;1.5708rad)
  Radius = 3
  SecondAngle = 0
FEATURE [Part::Compound] Compound
  Links = -> [Cylinder001]
  Placement = pos=(0,0,0) rot=(0,1,0;1.5708rad)
FEATURE [Part::Cylinder] Cylinder002  label="Zylinder002"
  Angle = 360
  AttacherType = Attacher::AttachEngine3D
  FirstAngle = 0
  Height = 317.7
  Placement = pos=(-30,12.7,-30) rot=(1,0,0;1.5708rad)
  Radius = 3
  SecondAngle = 0
FEATURE [Part::Compound] Compound001
  Links = -> [Cylinder002]
  Placement = pos=(0,0,0) rot=(0,1,0;3.14159rad)
FEATURE [Part::Cylinder] Cylinder003  label="Zylinder003"
  Angle = 360
  AttacherType = Attacher::AttachEngine3D
  FirstAngle = 0
  Height = 317.7
  Placement = pos=(-30,12.7,-30) rot=(1,0,0;1.5708rad)
  Radius = 3
  SecondAngle = 0
FEATURE [Part::Compound] Compound002
  Links = -> [Cylinder003]
  Placement = pos=(0,0,0) rot=(0,-1,0;1.5708rad)
FEATURE [Part::Compound] Compound003  label="ThreadedRodsM6"
  Links = -> [Compound002,Compound,Compound001,Cylinder]
  Placement = pos=(0,20,0) rot=(0,0,1;0rad)
FEATURE [Part::Box] Box  label="Würfel"
  AttacherType = Attacher::AttachEngine3D
  Height = 2.8
  Length = 90
  Placement = pos=(-45,-10,-11.5) rot=(0,0,1;0rad)
  Width = 220
FEATURE [Part::Box] Box001  label="Würfel001"
  AttacherType = Attacher::AttachEngine3D
  Height = 100
  Length = 100
  Placement = pos=(-50,0,-50) rot=(0,0,1;0rad)
  Width = 2.5
FEATURE [Part::Compound] Compound004
  Links = -> [Compound003,Box]
FEATURE [Part::Cut] Cut
  Base = -> Box001
  Tool = -> Compound004
FEATURE [Part::Cylinder] Cylinder004  label="Zylinder004"
  Angle = 360
  AttacherType = Attacher::AttachEngine3D
  FirstAngle = 0
  Height = 10
  Placement = pos=(0,6,0) rot=(1,0,0;1.5708rad)
  Radius = 37
  SecondAngle = 0
FEATURE [Part::Cut] Cut001
  Base = -> Cut
  Tool = -> Cylinder004
FEATURE [Part::Cylinder] Cylinder005  label="Zylinder005"
  Angle = 360
  AttacherType = Attacher::AttachEngine3D
  FirstAngle = 0
  Height = 10
  Placement = pos=(0,6,0) rot=(1,0,0;1.5708rad)
  Radius = 50
  SecondAngle = 0
FEATURE [Part::MultiCommon] Common
  Shapes = -> [Cut001,Cylinder005]
FEATURE [Part::Feature] Common_solid  label="Common (Solid)"
  shape: bbox 100 x 2.5 x 100 mm, 19 faces (baked)
